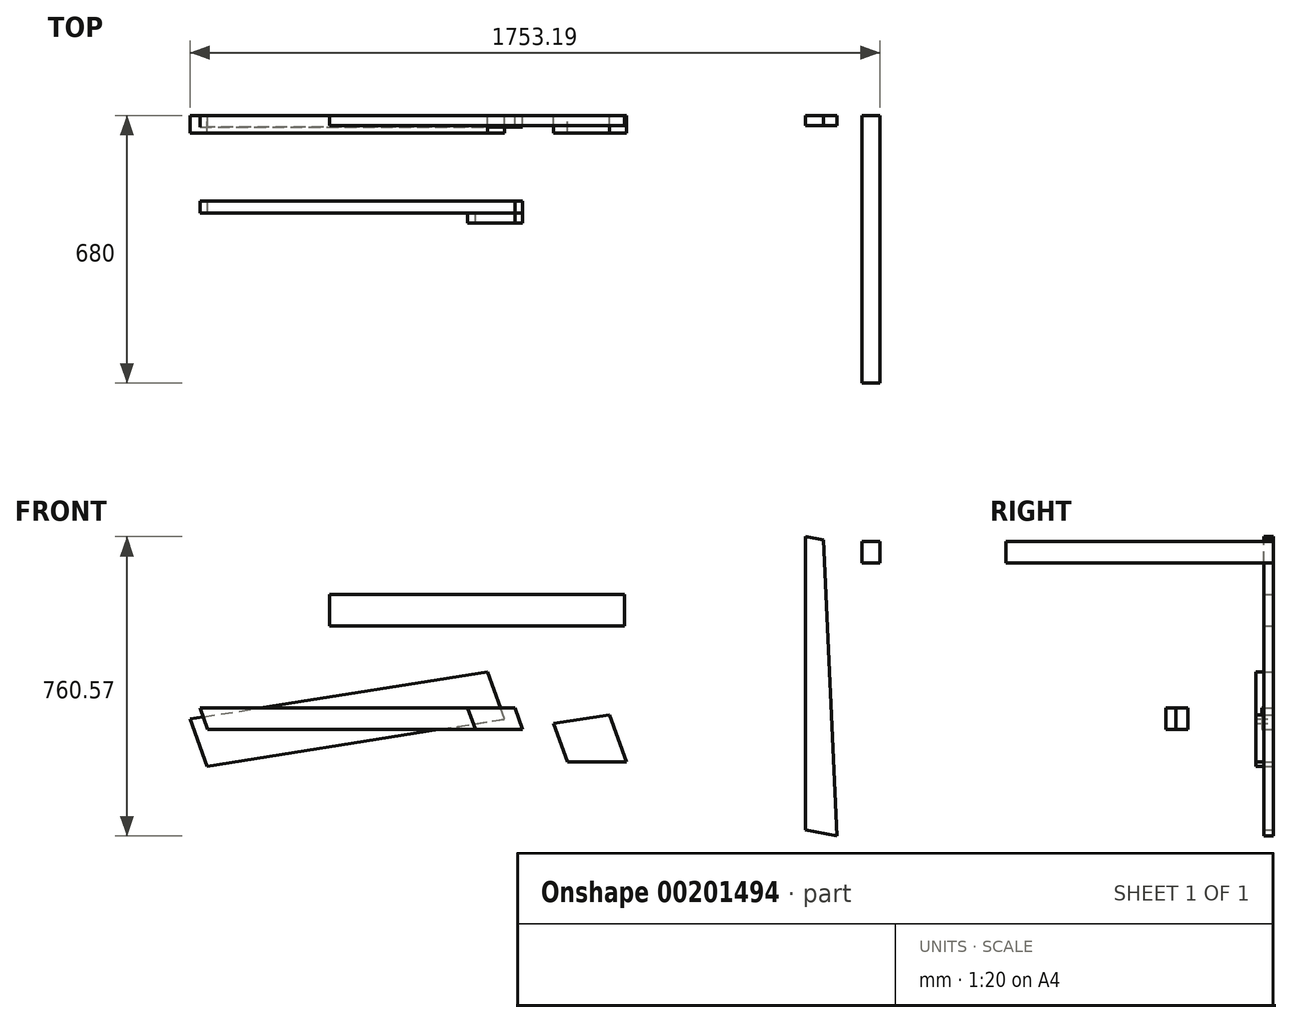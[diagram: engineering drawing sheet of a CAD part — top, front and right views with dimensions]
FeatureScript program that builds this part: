
annotation { "Feature Type Name" : "Feature", "Feature Type Description" : "" }
export const myFeature = defineFeature(function(context is Context, id is Id, definition is map)
    precondition{}
    {
        {
            var Q0;
            Q0=qCreatedBy(makeId("Front.planeOp"),FACE);
            var sketch = newSketch(context, id + "F0", { "sketchPlane" : qUnion([Q0])});
            skLineSegment(sketch, "E0.bottom", {"start": v(-271.79, 295.14) * mm, "end": v(478.21, 295.14) * mm});
            skLineSegment(sketch, "E0.top", {"start": v(-271.79, 215.14) * mm, "end": v(478.21, 215.14) * mm});
            skLineSegment(sketch, "E0.left", {"start": v(-271.79, 295.14) * mm, "end": v(-271.79, 215.14) * mm});
            skLineSegment(sketch, "E0.right", {"start": v(478.21, 295.14) * mm, "end": v(478.21, 215.14) * mm});
            skSolve(sketch);
        }
        {
            var Q0;
            Q0=makeQuery(id+"F0.imprint","IMPRINT",FACE,{"disambiguationData":[TD([[makeQuery(id+"F0.imprint","IMPRINT",EDGE,{"derivedFrom":sQuery(id+"F0.wireOp",EDGE,"E0.bottom")}),-1.0]])]});
            extrude(context, id + "F1", {"entities" : qUnion([Q0]), "depth" : 25 * mm});
        }
        {
            var Q0;
            Q0=qCreatedBy(makeId("Front.planeOp"),FACE);
            var sketch = newSketch(context, id + "F2", { "sketchPlane" : qUnion([Q0])});
            skLineSegment(sketch, "E1.bottom", {"start": v(-601.06, 6.51) * mm, "end": v(198.94, 6.51) * mm});
            skLineSegment(sketch, "E2", {"start": v(-601.06, 6.51) * mm, "end": v(-581.04, -48.49) * mm});
            skLineSegment(sketch, "E3", {"start": v(198.94, 6.51) * mm, "end": v(218.96, -48.49) * mm});
            skLineSegment(sketch, "E4", {"start": v(218.96, -48.49) * mm, "end": v(-581.04, -48.49) * mm});
            skSolve(sketch);
        }
        {
            var Q0;
            Q0=makeQuery(id+"F2.imprint","IMPRINT",FACE,{"disambiguationData":[TD([[makeQuery(id+"F2.imprint","IMPRINT",EDGE,{"derivedFrom":sQuery(id+"F2.wireOp",EDGE,"E1.bottom")}),-1.0]])]});
            extrude(context, id + "F3", {"entities" : qUnion([Q0]), "depth" : 30 * mm});
        }
        {
            var Q0;
            Q0=makeQuery(id+"F3.opExtrude","SWEPT_BODY",BODY,{"disambiguationData":[OSD([sQuery(id+"F2.wireOp",EDGE,"E1.bottom"),sQuery(id+"F2.wireOp",EDGE,"E2"),sQuery(id+"F2.wireOp",EDGE,"E3"),sQuery(id+"F2.wireOp",EDGE,"E4")])]});
            transform(context, id + "F4", {"entities" : qUnion([Q0]), "transformType" : TransformType.TRANSLATION_3D, "dx" : 0 * mm, "dy" : -218 * mm, "dz" : 0 * mm, "makeCopy" : true});
        }
        {
            var Q0;
            Q0=makeQuery(id+"F4.opPattern","COPY",FACE,{"derivedFrom":makeQuery(id+"F3.opExtrude","CAP_FACE",FACE,{"disambiguationData":[OSD([sQuery(id+"F2.wireOp",EDGE,"E1.bottom"),sQuery(id+"F2.wireOp",EDGE,"E2"),sQuery(id+"F2.wireOp",EDGE,"E3"),sQuery(id+"F2.wireOp",EDGE,"E4")])],"isStart":false}),"instanceName":"1"});
            var sketch = newSketch(context, id + "F5", { "sketchPlane" : qUnion([Q0])});
            skLineSegment(sketch, "E5", {"start": v(218.96, -48.49) * mm, "end": v(98.96, -48.49) * mm});
            skLineSegment(sketch, "E6", {"start": v(98.96, -48.49) * mm, "end": v(78.94, 6.51) * mm});
            skSolve(sketch);
        }
        {
            var Q0;
            Q0=makeQuery(id+"F5.imprint","IMPRINT",FACE,{"disambiguationData":[TD([[makeQuery(id+"F5.imprint","IMPRINT",EDGE,{"derivedFrom":sQuery(id+"F5.wireOp",EDGE,"E5")}),-1.0]])]});
            extrude(context, id + "F6", {"entities" : qUnion([Q0]), "depth" : 25 * mm});
        }
        {
            var Q0;
            Q0=qCreatedBy(makeId("Front.planeOp"),FACE);
            var sketch = newSketch(context, id + "F7", { "sketchPlane" : qUnion([Q0])});
            skLineSegment(sketch, "E7", {"start": v(-582.87, -141.77) * mm, "end": v(173.45, -21.77) * mm});
            skLineSegment(sketch, "E8", {"start": v(-626.55, -21.77) * mm, "end": v(129.77, 98.23) * mm});
            skLineSegment(sketch, "E9", {"start": v(-582.87, -141.77) * mm, "end": v(-626.55, -21.77) * mm});
            skLineSegment(sketch, "E10", {"start": v(173.45, -21.77) * mm, "end": v(129.77, 98.23) * mm});
            skSolve(sketch);
        }
        {
            var Q0;
            Q0=qCreatedBy(makeId("Front.planeOp"),FACE);
            var sketch = newSketch(context, id + "F8", { "sketchPlane" : qUnion([Q0])});
            skLineSegment(sketch, "E11", {"start": v(482.8, -130.76) * mm, "end": v(332.8, -130.76) * mm});
            skLineSegment(sketch, "E12", {"start": v(332.8, -130.76) * mm, "end": v(297.32, -33.26) * mm});
            skLineSegment(sketch, "E13", {"start": v(439.13, -10.76) * mm, "end": v(297.32, -33.26) * mm, "construction": true});
            skLineSegment(sketch, "E14", {"start": v(297.32, -33.26) * mm, "end": v(439.13, -10.76) * mm});
            skLineSegment(sketch, "E15", {"start": v(439.13, -10.76) * mm, "end": v(482.8, -130.76) * mm});
            skSolve(sketch);
        }
        {
            var Q0;
            Q0=makeQuery(id+"F8.imprint","IMPRINT",FACE,{"disambiguationData":[TD([[makeQuery(id+"F8.imprint","IMPRINT",EDGE,{"derivedFrom":sQuery(id+"F8.wireOp",EDGE,"E11")}),-1.0]])]});
            extrude(context, id + "F9", {"entities" : qUnion([Q0]), "depth" : 45 * mm});
        }
        {
            var Q0;
            Q0=makeQuery(id+"F7.imprint","IMPRINT",FACE,{"disambiguationData":[TD([[makeQuery(id+"F7.imprint","IMPRINT",EDGE,{"derivedFrom":sQuery(id+"F7.wireOp",EDGE,"E7")}),1.0]])]});
            extrude(context, id + "F10", {"entities" : qUnion([Q0]), "depth" : 45 * mm});
        }
        {
            var Q0;
            Q0=qCreatedBy(makeId("Front.planeOp"),FACE);
            var sketch = newSketch(context, id + "F11", { "sketchPlane" : qUnion([Q0])});
            skLineSegment(sketch, "E16", {"start": v(1017.59, -318.92) * mm, "end": v(983.5, 432.73) * mm});
            skLineSegment(sketch, "E17", {"start": v(983.5, 432.73) * mm, "end": v(937.59, 441.65) * mm});
            skLineSegment(sketch, "E18", {"start": v(1017.59, -318.92) * mm, "end": v(937.59, -303.39) * mm});
            skLineSegment(sketch, "E19", {"start": v(937.59, -303.39) * mm, "end": v(937.59, 441.65) * mm});
            skSolve(sketch);
        }
        {
            var Q0;
            Q0=makeQuery(id+"F11.imprint","IMPRINT",FACE,{"disambiguationData":[TD([[makeQuery(id+"F11.imprint","IMPRINT",EDGE,{"derivedFrom":sQuery(id+"F11.wireOp",EDGE,"E16")}),1.0]])]});
            extrude(context, id + "F12", {"entities" : qUnion([Q0]), "depth" : 25 * mm});
        }
        {
            var Q0;
            Q0=qCreatedBy(makeId("Front.planeOp"),FACE);
            var sketch = newSketch(context, id + "F13", { "sketchPlane" : qUnion([Q0])});
            skLineSegment(sketch, "E20", {"start": v(1126.64, 429.53) * mm, "end": v(1080.74, 429.53) * mm});
            skLineSegment(sketch, "E21", {"start": v(1080.74, 429.53) * mm, "end": v(1080.74, 374.53) * mm});
            skLineSegment(sketch, "E22", {"start": v(1080.74, 374.53) * mm, "end": v(1126.64, 374.53) * mm});
            skLineSegment(sketch, "E23", {"start": v(1126.64, 374.53) * mm, "end": v(1126.64, 429.53) * mm});
            skSolve(sketch);
        }
        {
            var Q0;
            Q0=makeQuery(id+"F13.imprint","IMPRINT",FACE,{"disambiguationData":[TD([[makeQuery(id+"F13.imprint","IMPRINT",EDGE,{"derivedFrom":sQuery(id+"F13.wireOp",EDGE,"E20")}),1.0]])]});
            extrude(context, id + "F14", {"entities" : qUnion([Q0]), "depth" : 680 * mm});
        }
    });
